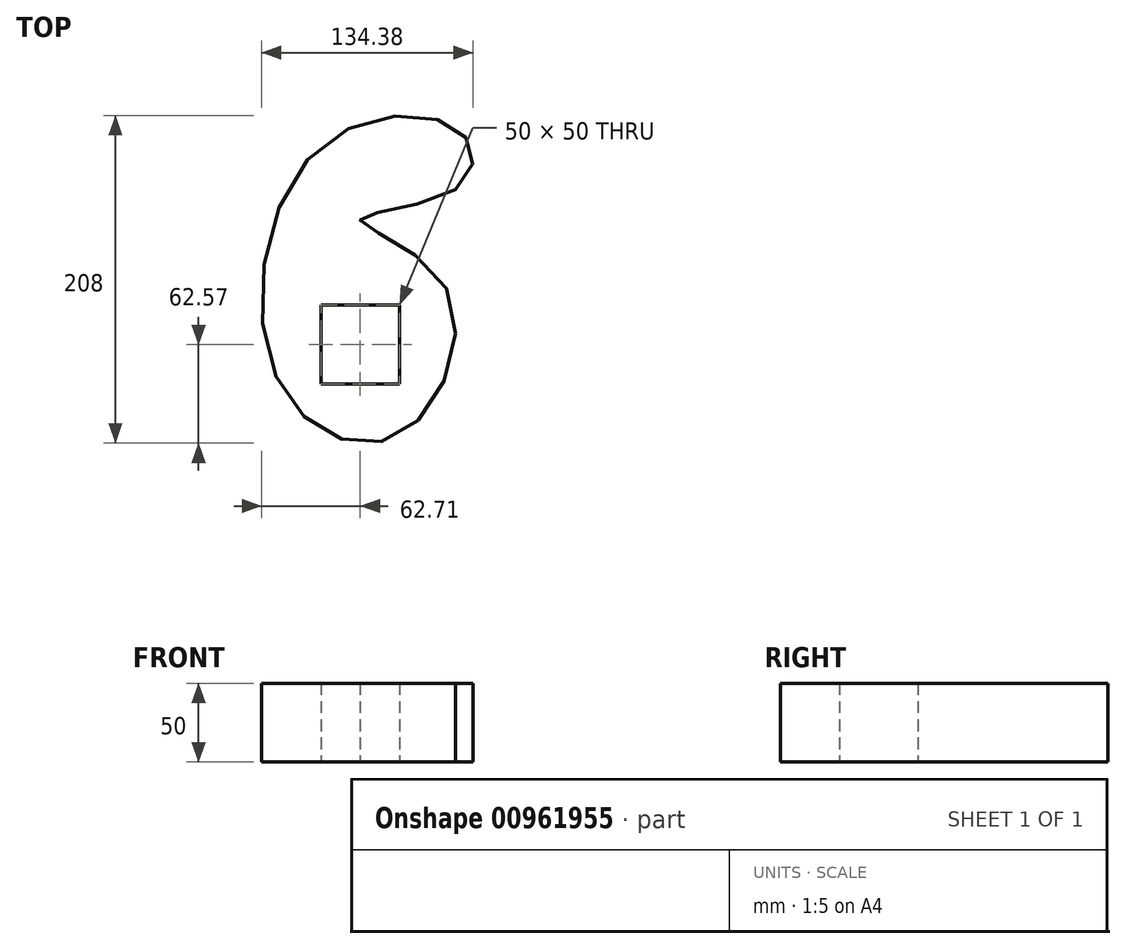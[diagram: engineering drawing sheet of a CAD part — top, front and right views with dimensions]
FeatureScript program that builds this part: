
annotation { "Feature Type Name" : "Feature", "Feature Type Description" : "" }
export const myFeature = defineFeature(function(context is Context, id is Id, definition is map)
    precondition{}
    {
        {
            var Q0;
            Q0=qCreatedBy(makeId("Top.planeOp"),FACE);
            var sketch = newSketch(context, id + "F0", { "sketchPlane" : qUnion([Q0])});
            skLineSegment(sketch, "E0.bottom", {"start": v(25, -25) * mm, "end": v(-25, -25) * mm});
            skLineSegment(sketch, "E0.top", {"start": v(25, 25) * mm, "end": v(-25, 25) * mm});
            skLineSegment(sketch, "E0.left", {"start": v(25, -25) * mm, "end": v(25, 25) * mm});
            skLineSegment(sketch, "E0.right", {"start": v(-25, -25) * mm, "end": v(-25, 25) * mm});
            skPoint(sketch, "E0.middle", {"position": v(0, 0) * mm});
            skPoint(sketch, "E1.1.internal.snap0", {"position": v(0, 25) * mm});
            skPoint(sketch, "E1.4.internal.snap0", {"position": v(0, -25) * mm});
            skFitSpline(sketch, "E1", {"points": [v(60.38, 98.57) * mm, v(0, 79.66) * mm, v(53.1, 38.56) * mm, v(25, -57.1) * mm, v(-51.29, -25) * mm, v(-25, 125.85) * mm, v(64.74, 134.22) * mm, v(60.38, 98.57) * mm]});
            skSolve(sketch);
        }
        {
            var Q0;
            Q0=qSketchRegion(id+"F0",true);
            extrude(context, id + "F1", {"entities" : qUnion([Q0]), "depth" : 50 * mm, "offsetDistance" : 25 * mm});
        }
        {
            var Q0;
            Q0=qSketchRegion(id+"F0",true);
            extrude(context, id + "F2", {"entities" : qUnion([Q0]), "operationType" : NewBodyOperationType.ADD, "depth" : 25 * mm, "offsetDistance" : 25 * mm});
        }
    });
